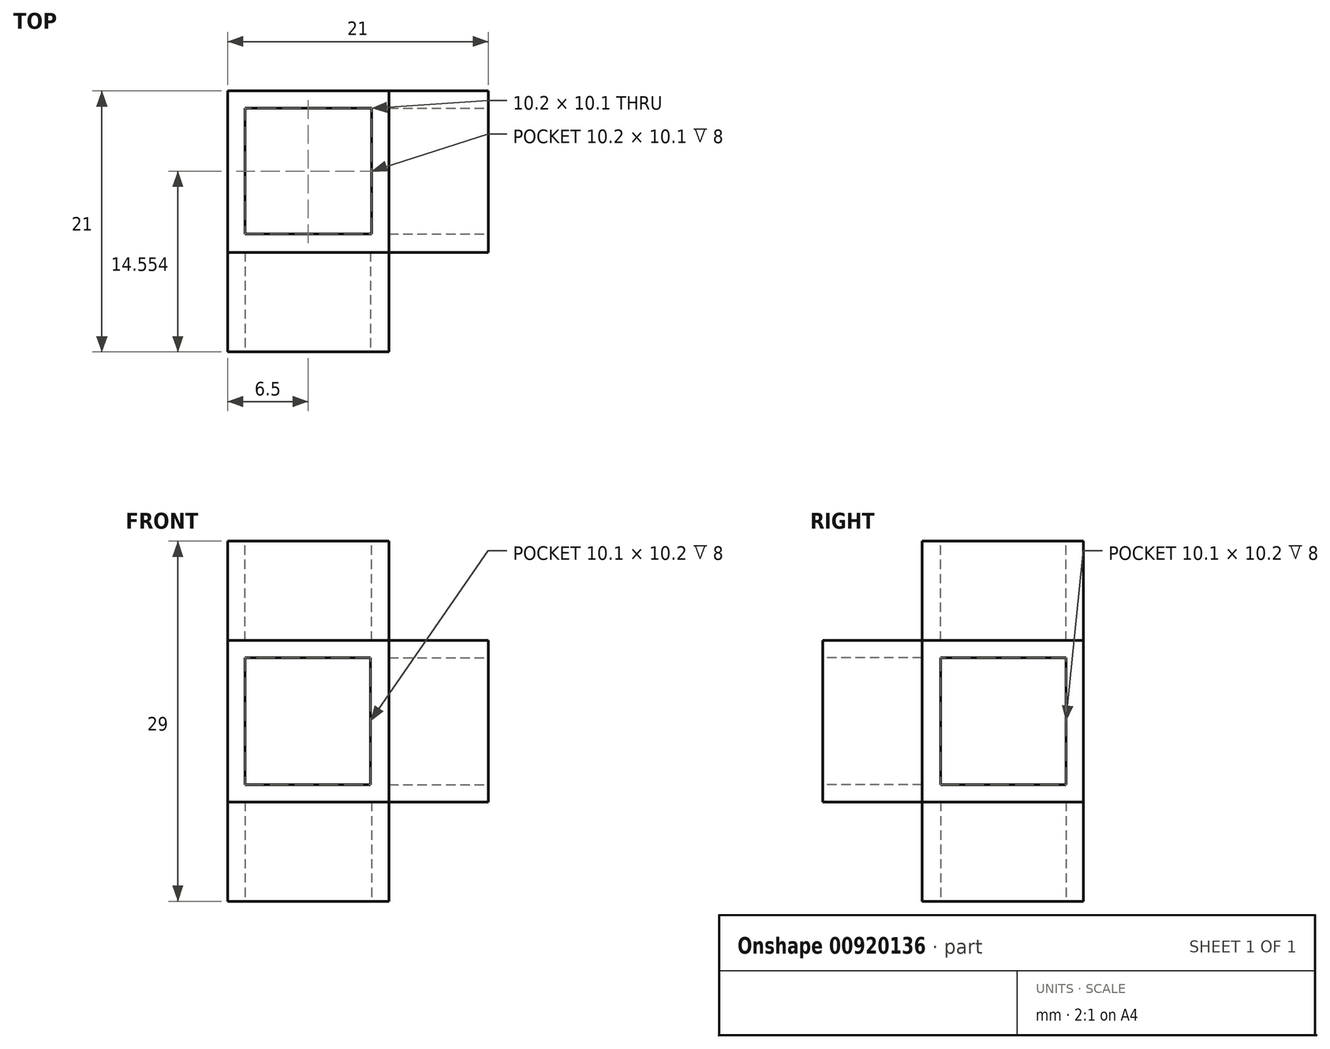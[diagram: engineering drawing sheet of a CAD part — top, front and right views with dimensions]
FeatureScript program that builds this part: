
annotation { "Feature Type Name" : "Feature", "Feature Type Description" : "" }
export const myFeature = defineFeature(function(context is Context, id is Id, definition is map)
    precondition{}
    {
        {
            var Q0;
            Q0=qCreatedBy(makeId("Top.planeOp"),FACE);
            var sketch = newSketch(context, id + "F0", { "sketchPlane" : qUnion([Q0])});
            skLineSegment(sketch, "E0.bottom", {"start": v(-28.43, 9.78) * mm, "end": v(-15.43, 9.78) * mm});
            skLineSegment(sketch, "E0.top", {"start": v(-28.43, -11.22) * mm, "end": v(-15.43, -11.22) * mm});
            skLineSegment(sketch, "E0.left", {"start": v(-28.43, 9.78) * mm, "end": v(-28.43, -11.22) * mm});
            skLineSegment(sketch, "E0.right", {"start": v(-15.43, 9.78) * mm, "end": v(-15.43, -11.22) * mm});
            skSolve(sketch);
        }
        {
            var Q0;
            Q0=makeQuery(id+"F0.imprint","IMPRINT",FACE,{"disambiguationData":[TD([[makeQuery(id+"F0.imprint","IMPRINT",EDGE,{"derivedFrom":sQuery(id+"F0.wireOp",EDGE,"E0.bottom")}),-1.0]])]});
            extrude(context, id + "F1", {"entities" : qUnion([Q0]), "depth" : 13 * mm, "offsetDistance" : 25 * mm});
        }
        {
            var Q0;
            Q0=makeQuery(id+"F1.opExtrude","SWEPT_FACE",FACE,{"disambiguationData":[OSD([sQuery(id+"F0.wireOp",EDGE,"E0.top")])]});
            var sketch = newSketch(context, id + "F2", { "sketchPlane" : qUnion([Q0])});
            skLineSegment(sketch, "E1.bottom", {"start": v(-27.03, 11.6) * mm, "end": v(-16.93, 11.6) * mm});
            skLineSegment(sketch, "E1.top", {"start": v(-27.03, 1.4) * mm, "end": v(-16.93, 1.4) * mm});
            skLineSegment(sketch, "E1.left", {"start": v(-27.03, 11.6) * mm, "end": v(-27.03, 1.4) * mm});
            skLineSegment(sketch, "E1.right", {"start": v(-16.93, 11.6) * mm, "end": v(-16.93, 1.4) * mm});
            skSolve(sketch);
        }
        {
            var Q0;
            Q0=makeQuery(id+"F1.opExtrude","CAP_FACE",FACE,{"disambiguationData":[OSD([sQuery(id+"F0.wireOp",EDGE,"E0.bottom"),sQuery(id+"F0.wireOp",EDGE,"E0.top"),sQuery(id+"F0.wireOp",EDGE,"E0.left"),sQuery(id+"F0.wireOp",EDGE,"E0.right")])],"isStart":false});
            var sketch = newSketch(context, id + "F3", { "sketchPlane" : qUnion([Q0])});
            skLineSegment(sketch, "E2.bottom", {"start": v(-28.43, 9.78) * mm, "end": v(-15.43, 9.78) * mm});
            skLineSegment(sketch, "E2.top", {"start": v(-28.43, -3.22) * mm, "end": v(-15.43, -3.22) * mm});
            skLineSegment(sketch, "E2.left", {"start": v(-28.43, 9.78) * mm, "end": v(-28.43, -3.22) * mm});
            skLineSegment(sketch, "E2.right", {"start": v(-15.43, 9.78) * mm, "end": v(-15.43, -3.22) * mm});
            skSolve(sketch);
        }
        {
            var Q0;
            Q0=makeQuery(id+"F3.imprint","IMPRINT",FACE,{"disambiguationData":[TD([[makeQuery(id+"F3.imprint","IMPRINT",EDGE,{"derivedFrom":sQuery(id+"F3.wireOp",EDGE,"E2.bottom")}),-1.0]])]});
            extrude(context, id + "F4", {"entities" : qUnion([Q0]), "operationType" : NewBodyOperationType.ADD, "depth" : 8 * mm, "offsetDistance" : 25 * mm, "hasSecondDirection" : true, "secondDirectionOppositeDirection" : true, "secondDirectionDepth" : 21 * mm});
        }
        {
            var Q0;
            Q0=makeQuery(id+"F4.opExtrude","CAP_FACE",FACE,{"disambiguationData":[OSD([sQuery(id+"F3.wireOp",EDGE,"E2.bottom"),sQuery(id+"F3.wireOp",EDGE,"E2.top"),sQuery(id+"F3.wireOp",EDGE,"E2.left"),sQuery(id+"F3.wireOp",EDGE,"E2.right")])],"isStart":false});
            var sketch = newSketch(context, id + "F5", { "sketchPlane" : qUnion([Q0])});
            skLineSegment(sketch, "E3.bottom", {"start": v(-27.03, 8.38) * mm, "end": v(-16.83, 8.38) * mm});
            skLineSegment(sketch, "E3.top", {"start": v(-27.03, -1.72) * mm, "end": v(-16.83, -1.72) * mm});
            skLineSegment(sketch, "E3.left", {"start": v(-27.03, 8.38) * mm, "end": v(-27.03, -1.72) * mm});
            skLineSegment(sketch, "E3.right", {"start": v(-16.83, 8.38) * mm, "end": v(-16.83, -1.72) * mm});
            skSolve(sketch);
        }
        {
            var Q0;
            Q0=makeQuery(id+"F5.imprint","IMPRINT",FACE,{"disambiguationData":[TD([[makeQuery(id+"F5.imprint","IMPRINT",EDGE,{"derivedFrom":sQuery(id+"F5.wireOp",EDGE,"E3.bottom")}),-1.0]])]});
            extrude(context, id + "F6", {"entities" : qUnion([Q0]), "operationType" : NewBodyOperationType.REMOVE, "oppositeDirection" : true, "depth" : 8 * mm, "offsetDistance" : 25 * mm});
        }
        {
            var Q0;
            Q0=makeQuery(id+"F4.opExtrude","CAP_FACE",FACE,{"disambiguationData":[OSD([sQuery(id+"F3.wireOp",EDGE,"E2.bottom"),sQuery(id+"F3.wireOp",EDGE,"E2.top"),sQuery(id+"F3.wireOp",EDGE,"E2.left"),sQuery(id+"F3.wireOp",EDGE,"E2.right")])],"isStart":true});
            var sketch = newSketch(context, id + "F7", { "sketchPlane" : qUnion([Q0])});
            skLineSegment(sketch, "E4.bottom", {"start": v(-16.83, 1.72) * mm, "end": v(-27.03, 1.72) * mm});
            skLineSegment(sketch, "E4.top", {"start": v(-16.83, -8.38) * mm, "end": v(-27.03, -8.38) * mm});
            skLineSegment(sketch, "E4.left", {"start": v(-16.83, 1.72) * mm, "end": v(-16.83, -8.38) * mm});
            skLineSegment(sketch, "E4.right", {"start": v(-27.03, 1.72) * mm, "end": v(-27.03, -8.38) * mm});
            skSolve(sketch);
        }
        {
            var Q0;
            Q0=makeQuery(id+"F7.imprint","IMPRINT",FACE,{"disambiguationData":[TD([[makeQuery(id+"F7.imprint","IMPRINT",EDGE,{"derivedFrom":sQuery(id+"F7.wireOp",EDGE,"E4.bottom")}),1.0]])]});
            extrude(context, id + "F8", {"entities" : qUnion([Q0]), "operationType" : NewBodyOperationType.REMOVE, "oppositeDirection" : true, "depth" : 8 * mm, "offsetDistance" : 25 * mm});
        }
        {
            var Q0;
            Q0=makeQuery(id+"F4.boolean.opBoolean","MERGE",FACE,{"derivedFrom":[makeQuery(id+"F1.opExtrude","SWEPT_FACE",FACE,{"disambiguationData":[OSD([sQuery(id+"F0.wireOp",EDGE,"E0.right")])]}),makeQuery(id+"F4.opExtrude","SWEPT_FACE",FACE,{"disambiguationData":[OSD([sQuery(id+"F3.wireOp",EDGE,"E2.right")])]})]});
            var sketch = newSketch(context, id + "F9", { "sketchPlane" : qUnion([Q0])});
            skLineSegment(sketch, "E5.bottom", {"start": v(9.78, 13) * mm, "end": v(-3.22, 13) * mm});
            skLineSegment(sketch, "E5.top", {"start": v(9.78, 0) * mm, "end": v(-3.22, 0) * mm});
            skLineSegment(sketch, "E5.left", {"start": v(9.78, 13) * mm, "end": v(9.78, 0) * mm});
            skLineSegment(sketch, "E5.right", {"start": v(-3.22, 13) * mm, "end": v(-3.22, 0) * mm});
            skSolve(sketch);
        }
        {
            var Q0;
            Q0=makeQuery(id+"F9.imprint","IMPRINT",FACE,{"disambiguationData":[TD([[makeQuery(id+"F9.imprint","IMPRINT",EDGE,{"derivedFrom":sQuery(id+"F9.wireOp",EDGE,"E5.bottom")}),1.0]])]});
            extrude(context, id + "F10", {"entities" : qUnion([Q0]), "operationType" : NewBodyOperationType.ADD, "depth" : 8 * mm, "offsetDistance" : 25 * mm});
        }
        {
            var Q0;
            Q0=makeQuery(id+"F10.opExtrude","CAP_FACE",FACE,{"disambiguationData":[OSD([sQuery(id+"F9.wireOp",EDGE,"E5.bottom"),sQuery(id+"F9.wireOp",EDGE,"E5.top"),sQuery(id+"F9.wireOp",EDGE,"E5.left"),sQuery(id+"F9.wireOp",EDGE,"E5.right")])],"isStart":false});
            var sketch = newSketch(context, id + "F11", { "sketchPlane" : qUnion([Q0])});
            skLineSegment(sketch, "E6.bottom", {"start": v(-1.72, 11.6) * mm, "end": v(8.38, 11.6) * mm});
            skLineSegment(sketch, "E6.top", {"start": v(-1.72, 1.4) * mm, "end": v(8.38, 1.4) * mm});
            skLineSegment(sketch, "E6.left", {"start": v(-1.72, 11.6) * mm, "end": v(-1.72, 1.4) * mm});
            skLineSegment(sketch, "E6.right", {"start": v(8.38, 11.6) * mm, "end": v(8.38, 1.4) * mm});
            skSolve(sketch);
        }
        {
            var Q0;
            Q0=makeQuery(id+"F2.imprint","IMPRINT",FACE,{"disambiguationData":[TD([[makeQuery(id+"F2.imprint","IMPRINT",EDGE,{"derivedFrom":sQuery(id+"F2.wireOp",EDGE,"E1.bottom")}),-1.0]])]});
            extrude(context, id + "F12", {"entities" : qUnion([Q0]), "operationType" : NewBodyOperationType.REMOVE, "oppositeDirection" : true, "depth" : 8 * mm, "offsetDistance" : 25 * mm});
        }
        {
            var Q0;
            Q0=makeQuery(id+"F11.imprint","IMPRINT",FACE,{"disambiguationData":[TD([[makeQuery(id+"F11.imprint","IMPRINT",EDGE,{"derivedFrom":sQuery(id+"F11.wireOp",EDGE,"E6.bottom")}),-1.0]])]});
            extrude(context, id + "F13", {"entities" : qUnion([Q0]), "operationType" : NewBodyOperationType.REMOVE, "oppositeDirection" : true, "depth" : 8 * mm, "offsetDistance" : 25 * mm});
        }
    });
